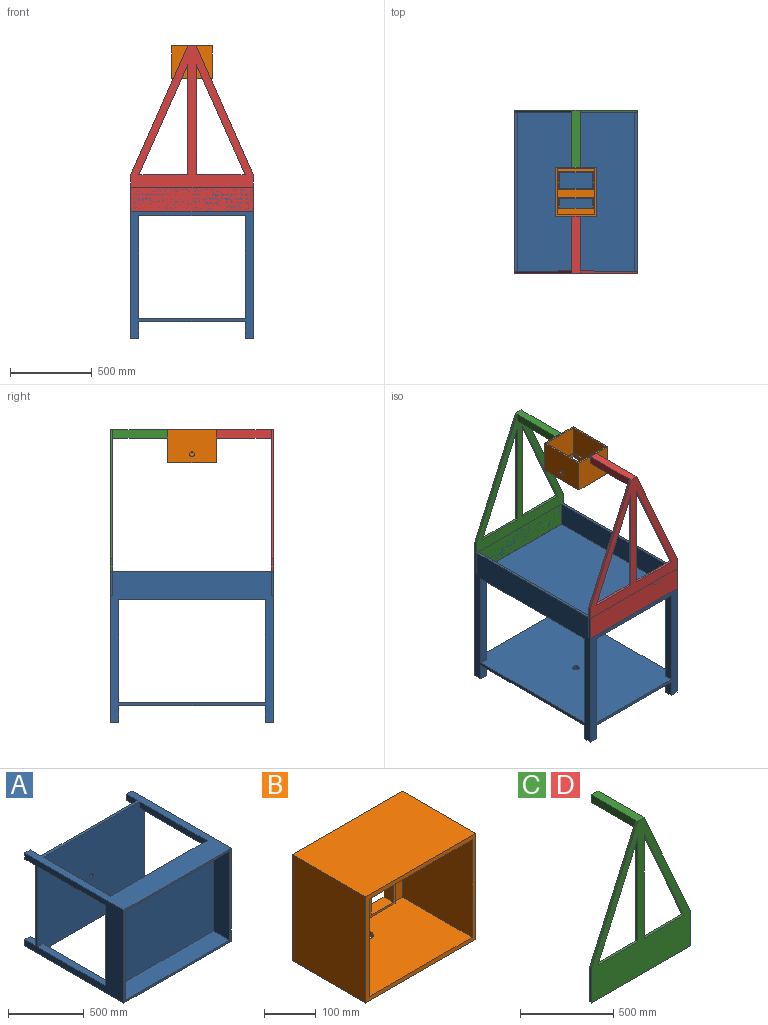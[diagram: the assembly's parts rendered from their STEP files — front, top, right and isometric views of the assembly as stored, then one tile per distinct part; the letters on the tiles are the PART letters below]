
ASSEMBLY  parts=4 mates=3
PART A: 34 faces, bbox 1000x925x750 mm
  f0: plane 630x50mm, normal (0,0,1), area 31500mm2, adj f1,f8,f10,f32
  f1: plane 630x50mm, normal (-1,0,0), area 31500mm2, adj f0,f8,f9,f32
  f2: plane 630x50mm, normal (1,0,0), area 31500mm2, adj f3,f8,f9,f32
  f3: plane 630x50mm, normal (0,0,1), area 31500mm2, adj f2,f8,f12,f32
  f4: plane 630x50mm, normal (0,0,-1), area 31500mm2, adj f5,f8,f10,f32
  f5: plane 630x50mm, normal (-1,0,0), area 31500mm2, adj f4,f8,f11,f32
  f6: plane 630x50mm, normal (1,0,0), area 31500mm2, adj f7,f8,f11,f32
  f7: plane 630x50mm, normal (0,0,-1), area 31500mm2, adj f6,f8,f12,f32
  f8: plane 1000x750mm, normal (0,1,0), area 740000mm2, adj f0,f1,f2,f3,f4,f5,f6,f7
  f9: plane 1000x925mm, normal (0,0,-1), area 268000mm2, adj f1,f2,f8,f10,f12,f14,f15,f16
  f10: plane 925x750mm, normal (1,0,0), area 219250mm2, adj f0,f4,f8,f9,f11,f13,f15,f19
  f11: plane 1000x925mm, normal (0,0,1), area 268000mm2, adj f5,f6,f8,f10,f12,f20,f21,f22
  f12: plane 925x750mm, normal (-1,0,0), area 219250mm2, adj f3,f7,f8,f9,f11,f17,f18,f23
  f13: plane 100x50mm, normal (0,0,1), area 5000mm2, adj f10,f14,f15,f31
  f14: plane 100x50mm, normal (-1,0,0), area 5000mm2, adj f9,f13,f15,f31
  f15: plane 50x50mm, normal (0,1,0), area 2500mm2, adj f9,f10,f13,f14
  f16: plane 100x50mm, normal (1,0,0), area 5000mm2, adj f9,f17,f18,f31
  f17: plane 100x50mm, normal (0,0,1), area 5000mm2, adj f12,f16,f18,f31
  f18: plane 50x50mm, normal (0,1,0), area 2500mm2, adj f9,f12,f16,f17
  f19: plane 100x50mm, normal (0,0,-1), area 5000mm2, adj f10,f20,f21,f31
  f20: plane 100x50mm, normal (-1,0,0), area 5000mm2, adj f11,f19,f21,f31
  f21: plane 50x50mm, normal (0,1,0), area 2500mm2, adj f10,f11,f19,f20
  f22: plane 100x50mm, normal (1,0,0), area 5000mm2, adj f11,f23,f24,f31
  f23: plane 100x50mm, normal (0,0,-1), area 5000mm2, adj f12,f22,f24,f31
  f24: plane 50x50mm, normal (0,1,0), area 2500mm2, adj f11,f12,f22,f23
  f25: plane 970x150mm, normal (0,0,1), area 145500mm2, adj f26,f28,f29,f30
  f26: plane 720x150mm, normal (1,0,0), area 108000mm2, adj f25,f27,f29,f30
  f27: plane 970x150mm, normal (0,0,-1), area 145500mm2, adj f26,f28,f29,f30
  f28: plane 720x150mm, normal (-1,0,0), area 108000mm2, adj f25,f27,f29,f30
  f29: plane 1000x750mm, normal (0,-1,0), area 51600mm2, adj f9,f10,f11,f12,f25,f26,f27,f28
  f30: plane 970x720mm, normal (0,-1,0), area 698400mm2, adj f25,f26,f27,f28
  f31: plane 1000x750mm, normal (0,1,0), area 738743.4mm2, adj f9,f10,f11,f12,f13,f14,f16,f17
  f32: plane 1000x750mm, normal (0,-1,0), area 738743.4mm2, adj f0,f1,f2,f3,f4,f5,f6,f7
  f33: cylinder r=20mm len=40mm, axis (0,1,0), area 2513.3mm2, adj f31,f32
PART B: 30 faces, bbox 300x200x250 mm
  f0: plane 300x250mm, normal (0,1,0), area 43000mm2, adj f2,f3,f4,f5,f14,f15,f16,f17
  f1: plane 280x230mm, normal (0,-1,0), area 26600mm2, adj f6,f7,f8,f9,f11,f12,f13,f18
  f2: plane 300x200mm, normal (0,0,-1), area 59293.1mm2, adj f0,f3,f5,f10,f29
  f3: plane 250x200mm, normal (1,0,0), area 50000mm2, adj f0,f2,f4,f10
  f4: plane 300x200mm, normal (0,0,1), area 60000mm2, adj f0,f3,f5,f10
  f5: plane 250x200mm, normal (-1,0,0), area 50000mm2, adj f0,f2,f4,f10
  f6: plane 280x190mm, normal (0,0,1), area 52493.1mm2, adj f1,f7,f9,f10,f29
  f7: plane 230x190mm, normal (1,0,0), area 43700mm2, adj f1,f6,f8,f10
  f8: plane 280x190mm, normal (0,0,-1), area 53200mm2, adj f1,f7,f9,f10
  f9: plane 230x190mm, normal (-1,0,0), area 43700mm2, adj f1,f6,f8,f10
  f10: plane 300x250mm, normal (0,-1,0), area 10600mm2, adj f2,f3,f4,f5,f6,f7,f8,f9
  f11: plane 210x15mm, normal (-1,0,0), area 3150mm2, adj f1,f12,f18,f19
  f12: plane 70x15mm, normal (0,0,-1), area 1050mm2, adj f1,f11,f13,f19
  f13: plane 210x15mm, normal (1,0,0), area 3150mm2, adj f1,f12,f18,f19
  f14: plane 200x25mm, normal (1,0,0), area 5000mm2, adj f0,f15,f17,f19
  f15: plane 60x25mm, normal (0,0,-1), area 1500mm2, adj f0,f14,f16,f19
  f16: plane 200x25mm, normal (-1,0,0), area 5000mm2, adj f0,f15,f17,f19
  f17: plane 60x25mm, normal (0,0,1), area 1500mm2, adj f0,f14,f16,f19
  f18: plane 70x15mm, normal (0,0,1), area 1050mm2, adj f1,f11,f13,f19
  f19: plane 210x70mm, normal (0,-1,0), area 2700mm2, adj f11,f12,f13,f14,f15,f16,f17,f18
  f20: plane 210x15mm, normal (1,0,0), area 3150mm2, adj f1,f21,f27,f28
  f21: plane 110x15mm, normal (0,0,1), area 1650mm2, adj f1,f20,f22,f28
  f22: plane 210x15mm, normal (-1,0,0), area 3150mm2, adj f1,f21,f27,f28
  f23: plane 200x25mm, normal (-1,0,0), area 5000mm2, adj f0,f24,f26,f28
  f24: plane 100x25mm, normal (0,0,1), area 2500mm2, adj f0,f23,f25,f28
  f25: plane 200x25mm, normal (1,0,0), area 5000mm2, adj f0,f24,f26,f28
  f26: plane 100x25mm, normal (0,0,-1), area 2500mm2, adj f0,f23,f25,f28
  f27: plane 110x15mm, normal (0,0,-1), area 1650mm2, adj f1,f20,f22,f28
  f28: plane 210x110mm, normal (0,-1,0), area 3100mm2, adj f20,f21,f22,f23,f24,f25,f26,f27
  f29: cylinder r=15mm len=30mm, axis (0,0,-1), area 942.5mm2, adj f2,f6
PART C: 18 faces, bbox 750x350x1015 mm
  f0: plane 335x50mm, normal (-1,0,0), area 16750mm2, adj f1,f3,f4,f16
  f1: plane 335x50mm, normal (0,0,-1), area 16750mm2, adj f0,f2,f4,f16
  f2: plane 335x50mm, normal (1,0,0), area 16750mm2, adj f1,f3,f4,f16
  f3: plane 350x50mm, normal (0,0,1), area 17500mm2, adj f0,f2,f4,f5,f10,f14
  f4: plane 50x50mm, normal (0,1,0), area 2500mm2, adj f0,f1,f2,f3
  f5: plane 1015x750mm, normal (0,-1,0), area 281607.1mm2, adj f3,f6,f7,f8,f9,f10,f11,f12
  f6: plane 677.14x300mm, normal (0.91,0,-0.41), area 11109.3mm2, adj f5,f7,f15,f16
  f7: plane 677.14x15mm, normal (-1,0,0), area 10157.1mm2, adj f5,f6,f15,f16
  f8: plane 677.14x15mm, normal (1,0,0), area 10157.1mm2, adj f5,f9,f13,f16
  f9: plane 677.14x300mm, normal (-0.91,0,-0.41), area 11109.3mm2, adj f5,f8,f13,f16
  f10: plane 790x350mm, normal (-0.91,0,0.41), area 12960.9mm2, adj f3,f5,f11,f16
  f11: plane 225x15mm, normal (-1,0,0), area 3375mm2, adj f5,f10,f16,f17
  f12: plane 225x15mm, normal (1,0,0), area 3375mm2, adj f5,f14,f16,f17
  f13: plane 300x15mm, normal (0,0,1), area 4500mm2, adj f5,f8,f9,f16
  f14: plane 790x350mm, normal (0.91,0,0.41), area 12960.9mm2, adj f3,f5,f12,f16
  f15: plane 300x15mm, normal (0,0,1), area 4500mm2, adj f5,f6,f7,f16
  f16: plane 1015x750mm, normal (0,1,0), area 279107.1mm2, adj f0,f1,f2,f6,f7,f8,f9,f10
  f17: plane 750x15mm, normal (0,0,-1), area 11250mm2, adj f5,f11,f12,f16
PART D: same geometry as C
PLACE A rot(axis=(-0.58,-0.58,0.58),120deg) t=(0,500,-620)mm
PLACE B rot(axis=(-0.58,0.58,-0.58),120deg) t=(0,500,220)mm
PLACE C rot(axis=(0,0,1),180deg) t=(0,1000,0)mm
PLACE D at identity
MATE fastened A.f30 <-> D.f17  axis (0,0,1) through (0,15,-595)mm
MATE fastened B.f3 <-> D.f4  axis (0,-1,0) through (0,350,395)mm
MATE fastened C.f4 <-> B.f5  axis (0,-1,0) through (0,650,395)mm
